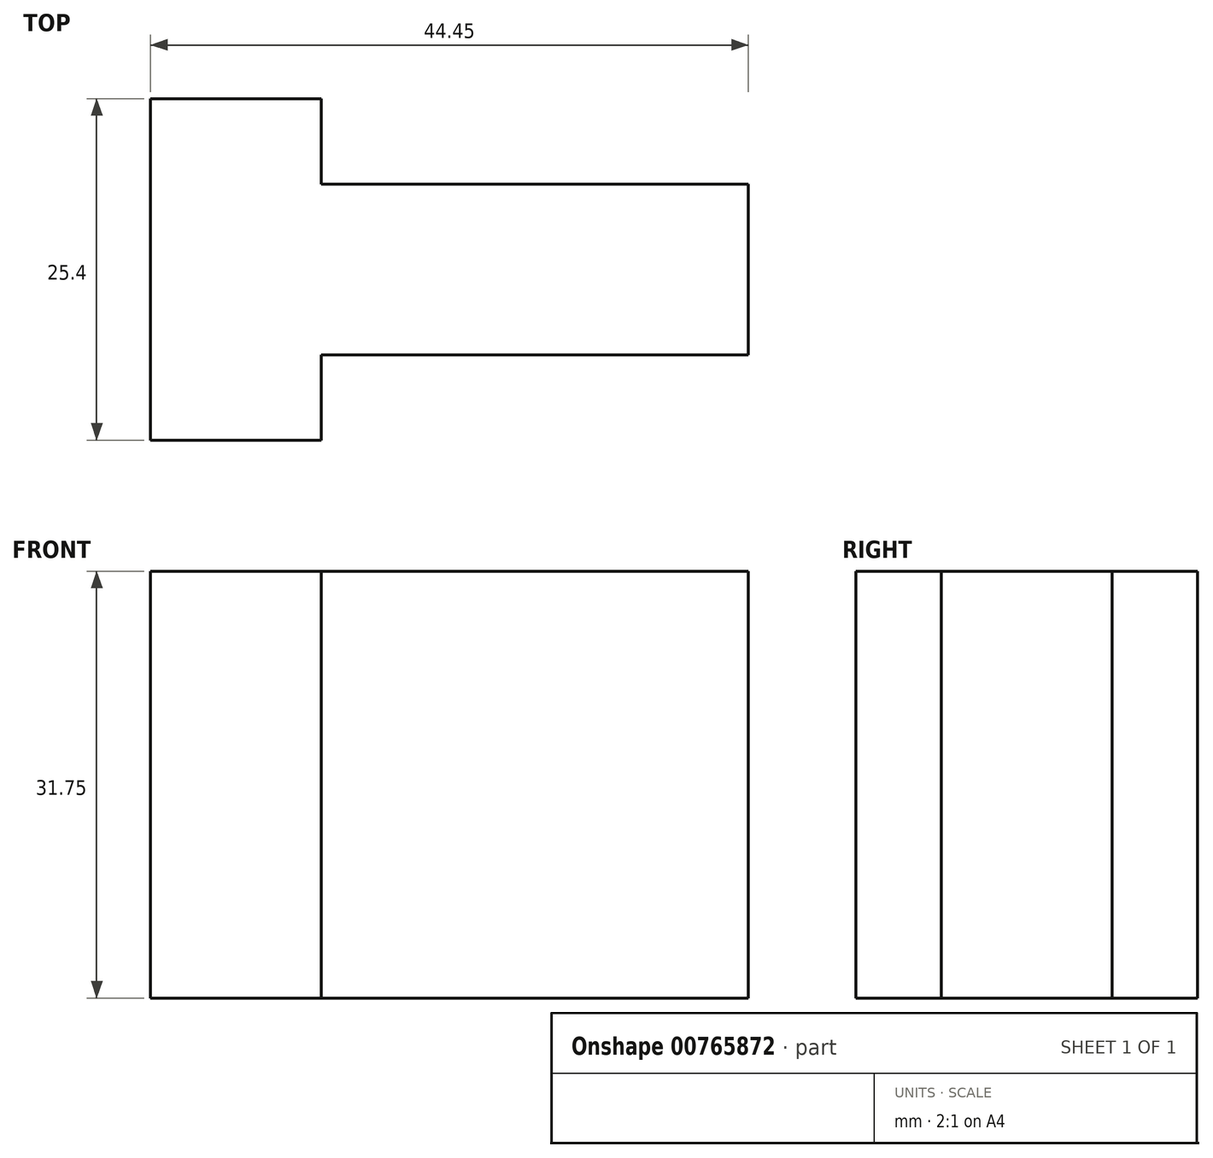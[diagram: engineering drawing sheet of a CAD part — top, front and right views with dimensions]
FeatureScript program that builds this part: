
annotation { "Feature Type Name" : "Feature", "Feature Type Description" : "" }
export const myFeature = defineFeature(function(context is Context, id is Id, definition is map)
    precondition{}
    {
        {
            var Q0;
            Q0=qCreatedBy(makeId("Top.planeOp"),FACE);
            var sketch = newSketch(context, id + "F0", { "sketchPlane" : qUnion([Q0])});
            skLineSegment(sketch, "E0", {"start": v(0, 0) * mm, "end": v(12.7, 0) * mm});
            skLineSegment(sketch, "E1", {"start": v(12.7, 0) * mm, "end": v(12.7, 6.35) * mm});
            skLineSegment(sketch, "E2", {"start": v(12.7, 6.35) * mm, "end": v(44.45, 6.35) * mm});
            skLineSegment(sketch, "E3", {"start": v(44.45, 6.35) * mm, "end": v(44.45, 19.05) * mm});
            skLineSegment(sketch, "E4", {"start": v(44.45, 19.05) * mm, "end": v(12.7, 19.05) * mm});
            skLineSegment(sketch, "E5", {"start": v(12.7, 19.05) * mm, "end": v(12.7, 25.4) * mm});
            skLineSegment(sketch, "E6", {"start": v(12.7, 25.4) * mm, "end": v(0, 25.4) * mm});
            skLineSegment(sketch, "E7", {"start": v(0, 25.4) * mm, "end": v(0, 0) * mm});
            skSolve(sketch);
        }
        {
            var Q0;
            Q0 = qSketchRegion(id + "F0", true);
            extrude(context, id + "F1", {"entities" : qUnion([Q0]), "depth" : 31.75 * mm, "offsetDistance" : 25.4 * mm});
        }
    });
